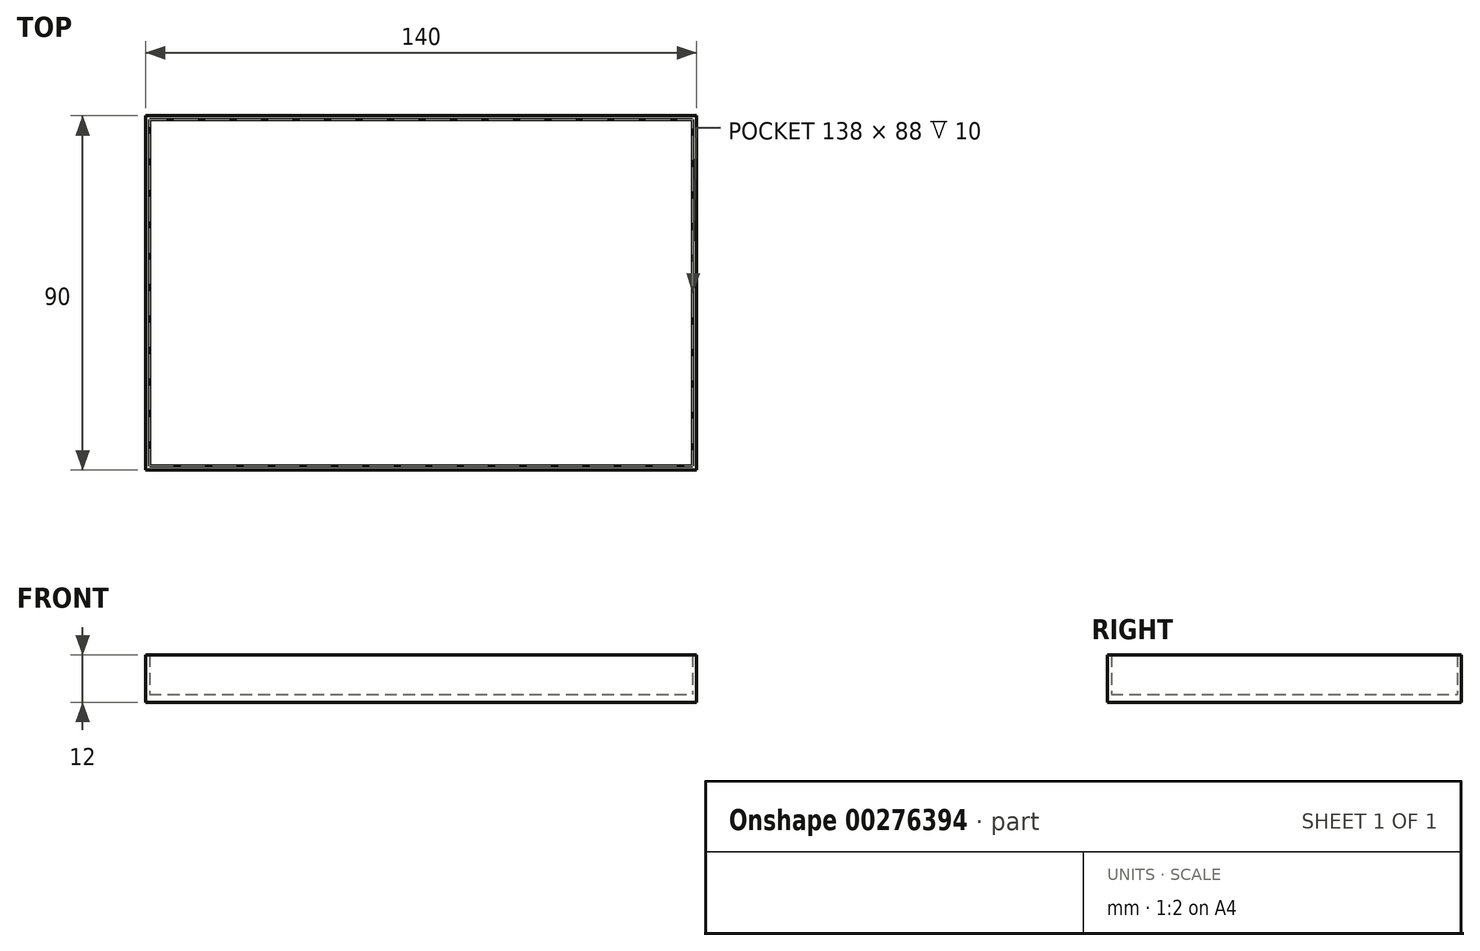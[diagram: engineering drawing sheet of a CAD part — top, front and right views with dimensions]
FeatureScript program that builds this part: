
annotation { "Feature Type Name" : "Feature", "Feature Type Description" : "" }
export const myFeature = defineFeature(function(context is Context, id is Id, definition is map)
    precondition{}
    {
        {
            var Q0;
            Q0=qCreatedBy(makeId("Top.planeOp"),FACE);
            var sketch = newSketch(context, id + "F0", { "sketchPlane" : qUnion([Q0])});
            skLineSegment(sketch, "E0.bottom", {"start": v(70, 45) * mm, "end": v(-70, 45) * mm});
            skLineSegment(sketch, "E0.top", {"start": v(70, -45) * mm, "end": v(-70, -45) * mm});
            skLineSegment(sketch, "E0.left", {"start": v(70, 45) * mm, "end": v(70, -45) * mm});
            skLineSegment(sketch, "E0.right", {"start": v(-70, 45) * mm, "end": v(-70, -45) * mm});
            skPoint(sketch, "E0.middle", {"position": v(0, 0) * mm});
            skLineSegment(sketch, "E1.0", {"start": v(69, 44) * mm, "end": v(-69, 44) * mm});
            skLineSegment(sketch, "E1.1", {"start": v(69, 44) * mm, "end": v(69, -44) * mm});
            skLineSegment(sketch, "E1.2", {"start": v(69, -44) * mm, "end": v(-69, -44) * mm});
            skLineSegment(sketch, "E1.3", {"start": v(-69, 44) * mm, "end": v(-69, -44) * mm});
            skSolve(sketch);
        }
        {
            var Q0;
            Q0 = qSketchRegion(id + "F0", true);
            var Q1;
            Q1=makeQuery(id+"F0.imprint","IMPRINT",FACE,{"disambiguationData":[TD([[makeQuery(id+"F0.imprint","IMPRINT",EDGE,{"derivedFrom":sQuery(id+"F0.wireOp",EDGE,"E1.0")}),1.0]])]});
            extrude(context, id + "F1", {"entities" : qUnion([Q0, Q1]), "depth" : 2 * mm});
        }
        {
            var Q0;
            Q0=makeQuery(id+"F0.imprint","IMPRINT",FACE,{"disambiguationData":[TD([[makeQuery(id+"F0.imprint","IMPRINT",EDGE,{"derivedFrom":sQuery(id+"F0.wireOp",EDGE,"E0.bottom")}),1.0]])]});
            extrude(context, id + "F2", {"entities" : qUnion([Q0]), "operationType" : NewBodyOperationType.ADD, "depth" : 12 * mm});
        }
    });
